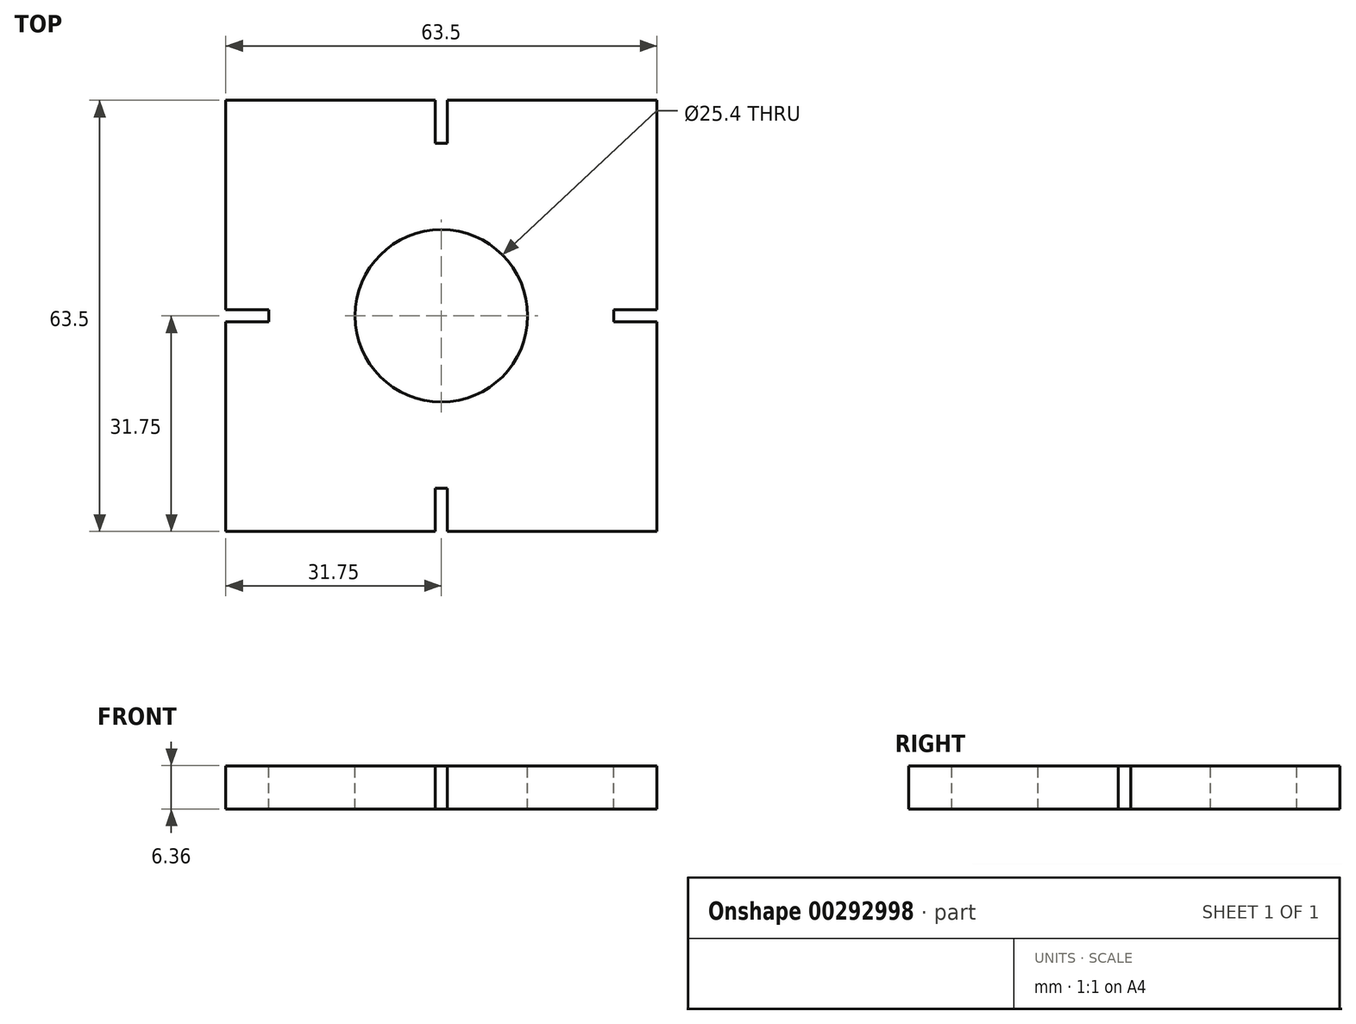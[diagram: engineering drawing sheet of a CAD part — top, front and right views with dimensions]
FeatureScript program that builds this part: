
annotation { "Feature Type Name" : "Feature", "Feature Type Description" : "" }
export const myFeature = defineFeature(function(context is Context, id is Id, definition is map)
    precondition{}
    {
        {
            var Q0;
            Q0=qCreatedBy(makeId("Top.planeOp"),FACE);
            var sketch = newSketch(context, id + "F0", { "sketchPlane" : qUnion([Q0])});
            skLineSegment(sketch, "E0.bottom", {"start": v(-31.75, 31.75) * mm, "end": v(31.75, 31.75) * mm});
            skLineSegment(sketch, "E0.top", {"start": v(-31.75, -31.75) * mm, "end": v(31.75, -31.75) * mm});
            skLineSegment(sketch, "E0.left", {"start": v(-31.75, 31.75) * mm, "end": v(-31.75, -31.75) * mm});
            skLineSegment(sketch, "E0.right", {"start": v(31.75, 31.75) * mm, "end": v(31.75, -31.75) * mm});
            skPoint(sketch, "E0.middle", {"position": v(0, 0) * mm});
            skSolve(sketch);
        }
        {
            var Q0;
            Q0 = qSketchRegion(id + "F0", true);
            extrude(context, id + "F1", {"entities" : qUnion([Q0]), "depth" : 3.17 * mm});
        }
        {
            var Q0;
            Q0=makeQuery(id+"F1.opExtrude","CAP_FACE",FACE,{"disambiguationData":[OSD([sQuery(id+"F0.wireOp",EDGE,"E0.bottom"),sQuery(id+"F0.wireOp",EDGE,"E0.top"),sQuery(id+"F0.wireOp",EDGE,"E0.left"),sQuery(id+"F0.wireOp",EDGE,"E0.right")])],"isStart":true});
            extrude(context, id + "F2", {"entities" : qUnion([Q0]), "operationType" : NewBodyOperationType.ADD, "depth" : 3.17 * mm});
        }
        {
            var Q0;
            Q0=makeQuery(id+"F1.opExtrude","CAP_FACE",FACE,{"disambiguationData":[OSD([sQuery(id+"F0.wireOp",EDGE,"E0.bottom"),sQuery(id+"F0.wireOp",EDGE,"E0.top"),sQuery(id+"F0.wireOp",EDGE,"E0.left"),sQuery(id+"F0.wireOp",EDGE,"E0.right")])],"isStart":false});
            var sketch = newSketch(context, id + "F3", { "sketchPlane" : qUnion([Q0])});
            skCircle(sketch, "E1", {"center": v(0, 0) * mm, "radius": 12.7 * mm});
            skLineSegment(sketch, "E2", {"start": v(0, 31.75) * mm, "end": v(0.89, 31.75) * mm});
            skLineSegment(sketch, "E3", {"start": v(0.89, 31.75) * mm, "end": v(-0.89, 31.75) * mm});
            skLineSegment(sketch, "E4", {"start": v(-0.89, 31.75) * mm, "end": v(-0.89, 25.4) * mm});
            skLineSegment(sketch, "E5", {"start": v(-0.89, 25.4) * mm, "end": v(0.89, 25.4) * mm});
            skLineSegment(sketch, "E6", {"start": v(0.89, 25.4) * mm, "end": v(0.89, 31.75) * mm});
            skLineSegment(sketch, "E7", {"start": v(31.75, 0) * mm, "end": v(31.75, 0.89) * mm});
            skLineSegment(sketch, "E8", {"start": v(31.75, 0.89) * mm, "end": v(31.75, -0.89) * mm});
            skLineSegment(sketch, "E9", {"start": v(31.75, -0.89) * mm, "end": v(25.4, -0.89) * mm});
            skLineSegment(sketch, "E10", {"start": v(25.4, -0.89) * mm, "end": v(25.4, 0.89) * mm});
            skLineSegment(sketch, "E11", {"start": v(25.4, 0.89) * mm, "end": v(31.75, 0.89) * mm});
            skLineSegment(sketch, "E12", {"start": v(0, -31.75) * mm, "end": v(-0.89, -31.75) * mm});
            skLineSegment(sketch, "E13", {"start": v(-0.89, -31.75) * mm, "end": v(0.89, -31.75) * mm});
            skLineSegment(sketch, "E14", {"start": v(0.89, -31.75) * mm, "end": v(0.89, -25.4) * mm});
            skLineSegment(sketch, "E15", {"start": v(0.89, -25.4) * mm, "end": v(-0.89, -25.4) * mm});
            skLineSegment(sketch, "E16", {"start": v(-0.89, -25.4) * mm, "end": v(-0.89, -31.75) * mm});
            skLineSegment(sketch, "E17", {"start": v(-31.75, 0) * mm, "end": v(-31.75, -0.89) * mm});
            skLineSegment(sketch, "E18", {"start": v(-31.75, -0.89) * mm, "end": v(-31.75, 0.89) * mm});
            skLineSegment(sketch, "E19", {"start": v(-31.75, 0.89) * mm, "end": v(-25.4, 0.89) * mm});
            skLineSegment(sketch, "E20", {"start": v(-25.4, 0.89) * mm, "end": v(-25.4, -0.89) * mm});
            skLineSegment(sketch, "E21", {"start": v(-25.4, -0.89) * mm, "end": v(-31.75, -0.89) * mm});
            skSolve(sketch);
        }
        {
            var Q0;
            Q0 = qSketchRegion(id + "F3", true);
            extrude(context, id + "F4", {"entities" : qUnion([Q0]), "operationType" : NewBodyOperationType.REMOVE, "oppositeDirection" : true, "depth" : 6.35 * mm});
        }
        {
            var Q0;
            Q0 = qSketchRegion(id + "F3", true);
            extrude(context, id + "F5", {"entities" : qUnion([Q0]), "operationType" : NewBodyOperationType.REMOVE, "oppositeDirection" : true, "depth" : 25.4 * mm});
        }
        {
            var Q0;
            Q0 = qSketchRegion(id + "F3", true);
            extrude(context, id + "F6", {"entities" : qUnion([Q0]), "operationType" : NewBodyOperationType.REMOVE, "oppositeDirection" : true, "depth" : 25.4 * mm});
        }
        {
            var Q0;
            Q0 = qSketchRegion(id + "F3", true);
            extrude(context, id + "F7", {"entities" : qUnion([Q0]), "operationType" : NewBodyOperationType.REMOVE, "oppositeDirection" : true, "depth" : 25.4 * mm});
        }
        {
            var Q0;
            Q0 = qSketchRegion(id + "F3", true);
            extrude(context, id + "F8", {"entities" : qUnion([Q0]), "operationType" : NewBodyOperationType.REMOVE, "oppositeDirection" : true, "depth" : 25.4 * mm});
        }
    });
